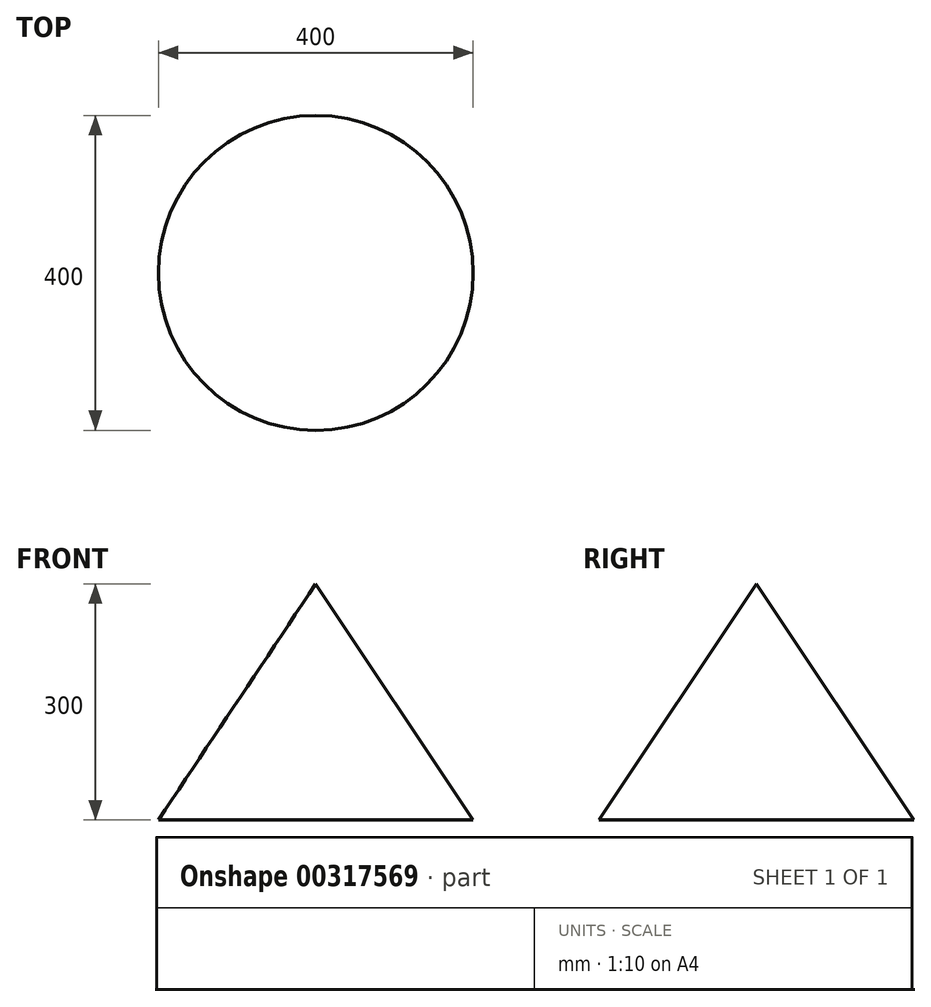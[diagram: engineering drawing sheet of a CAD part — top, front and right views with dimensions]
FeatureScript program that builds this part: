
annotation { "Feature Type Name" : "Feature", "Feature Type Description" : "" }
export const myFeature = defineFeature(function(context is Context, id is Id, definition is map)
    precondition{}
    {
        {
            var Q0;
            Q0=qCreatedBy(makeId("Front.planeOp"),FACE);
            var sketch = newSketch(context, id + "F0", { "sketchPlane" : qUnion([Q0])});
            skLineSegment(sketch, "E0", {"start": v(0, 0) * mm, "end": v(0, 300) * mm});
            skLineSegment(sketch, "E1", {"start": v(0, 300) * mm, "end": v(200, 0) * mm});
            skLineSegment(sketch, "E2", {"start": v(200, 0) * mm, "end": v(0, 0) * mm});
            skSolve(sketch);
        }
        {
            var Q0;
            Q0 = qSketchRegion(id + "F0", true);
            var Q1;
            Q1=sQuery(id+"F0.wireOp",EDGE,"E0");
            revolve(context, id + "F1", {"entities" : qUnion([Q0]), "axis" : qUnion([Q1]), "revolveType" : RevolveType.FULL});
        }
    });
